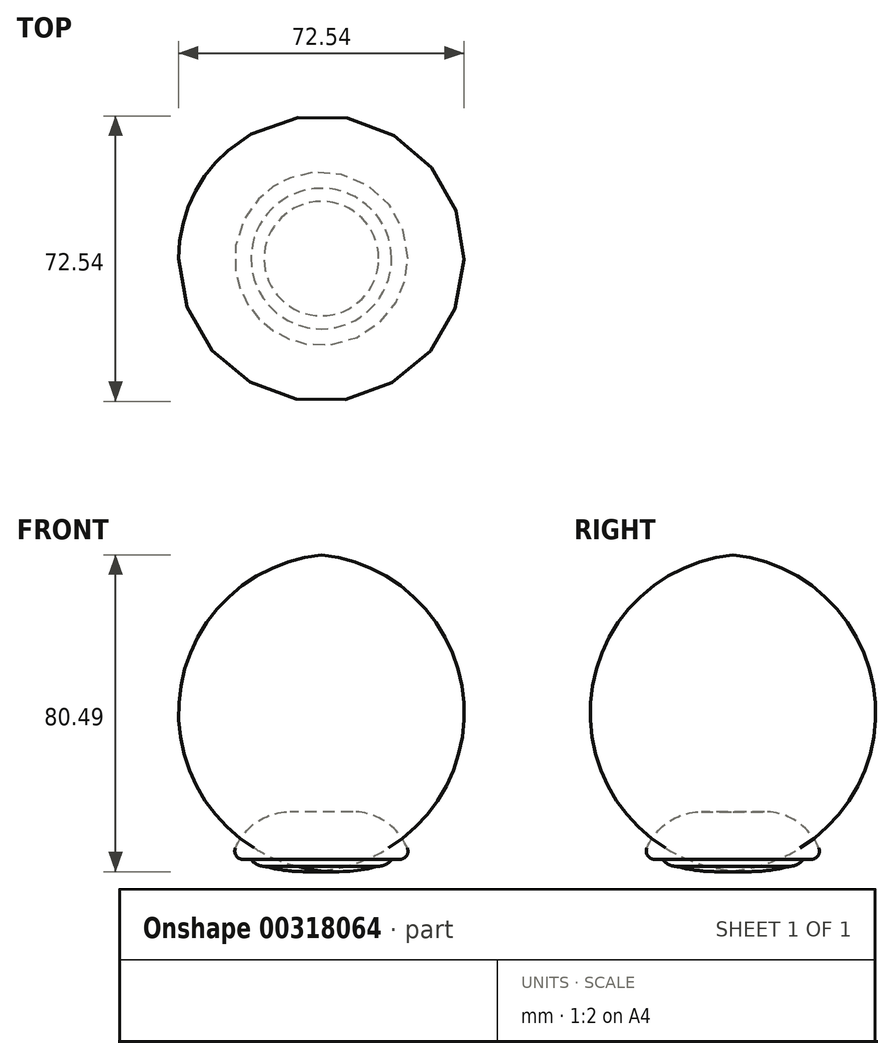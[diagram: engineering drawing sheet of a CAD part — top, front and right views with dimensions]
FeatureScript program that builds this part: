
annotation { "Feature Type Name" : "Feature", "Feature Type Description" : "" }
export const myFeature = defineFeature(function(context is Context, id is Id, definition is map)
    precondition{}
    {
        {
            var Q0;
            Q0=qCreatedBy(makeId("Front.planeOp"),FACE);
            var sketch = newSketch(context, id + "F0", { "sketchPlane" : qUnion([Q0])});
            skLineSegment(sketch, "E0", {"start": v(0, 0) * mm, "end": v(8, 0) * mm});
            skArc(sketch, "E1", {"start": v(21.84, -9.22) * mm, "mid": v(16.32, -2.52) * mm, "end": v(8, 0) * mm});
            skArc(sketch, "E2", {"start": v(14.55, -13.82) * mm, "mid": v(16.42, -13.35) * mm, "end": v(17.85, -12.06) * mm});
            skLineSegment(sketch, "E3", {"start": v(14.55, -13.82) * mm, "end": v(0, -13.82) * mm});
            skArc(sketch, "E4", {"start": v(21.84, -9.22) * mm, "mid": v(21.66, -11.15) * mm, "end": v(19.95, -12.06) * mm});
            skLineSegment(sketch, "E5", {"start": v(19.95, -12.06) * mm, "end": v(0, -12.06) * mm});
            skArc(sketch, "E6", {"start": v(0, -15) * mm, "mid": v(7.33, -15.07) * mm, "end": v(14.55, -13.82) * mm});
            skLineSegment(sketch, "E7", {"start": v(0, 0) * mm, "end": v(0, -15) * mm});
            skSolve(sketch);
        }
        {
            var Q0;
            Q0 = qSketchRegion(id + "F0", true);
            var Q1;
            Q1=sQuery(id+"F0.wireOp",EDGE,"E7");
            revolve(context, id + "F1", {"entities" : qUnion([Q0]), "axis" : qUnion([Q1]), "revolveType" : RevolveType.FULL});
        }
    });
